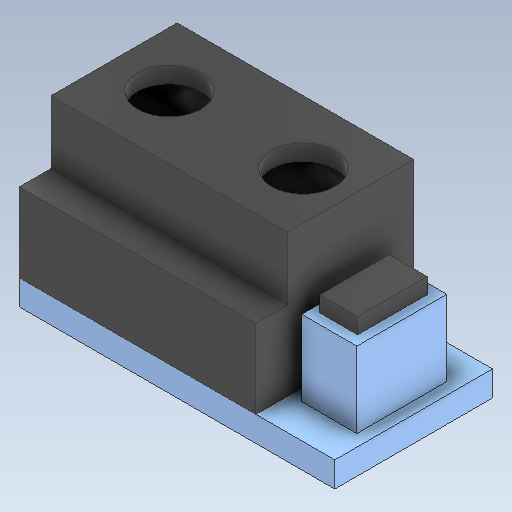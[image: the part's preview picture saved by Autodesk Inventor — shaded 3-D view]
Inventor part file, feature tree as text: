
AUTODESK INVENTOR PART (.ipt)
format: ipt  version: 2020 (Build 240168000, 168)  size: 172,032 bytes
history: native  units: in
note: dims shown in document units (in); Inventor stores cm internally (conversion verified against a paired STEP export)
features: sketch x7, other x4, plane x4
ambient origin geometry x8: Origin, YZ Plane, XZ Plane, XY Plane, X Axis, Y Axis, Z Axis, Center Point
bodies: Solid1 (feature_tree), Solid2 (feature_tree)
feature tree (15):
  other  "Sharp_Czujnik.ipt"
  other  "Bryła1::Sharp_Czujnik.ipt"
  other  "Solid2::Sharp_Czujnik.ipt"
  other  "TaggingFeature1"
  sketch  "Szkic1"
  sketch  "Szkic2"
  sketch  "Szkic3"
  sketch  "Sketch4"  dims[d0=0.3937in]
  sketch  "Sketch5"
  sketch  "Sketch7"
  sketch  "Sketch9"
  plane  "Work Plane1"
  plane  "Work Plane2"
  plane  "Work Plane3"
  plane  "Work Plane4"
